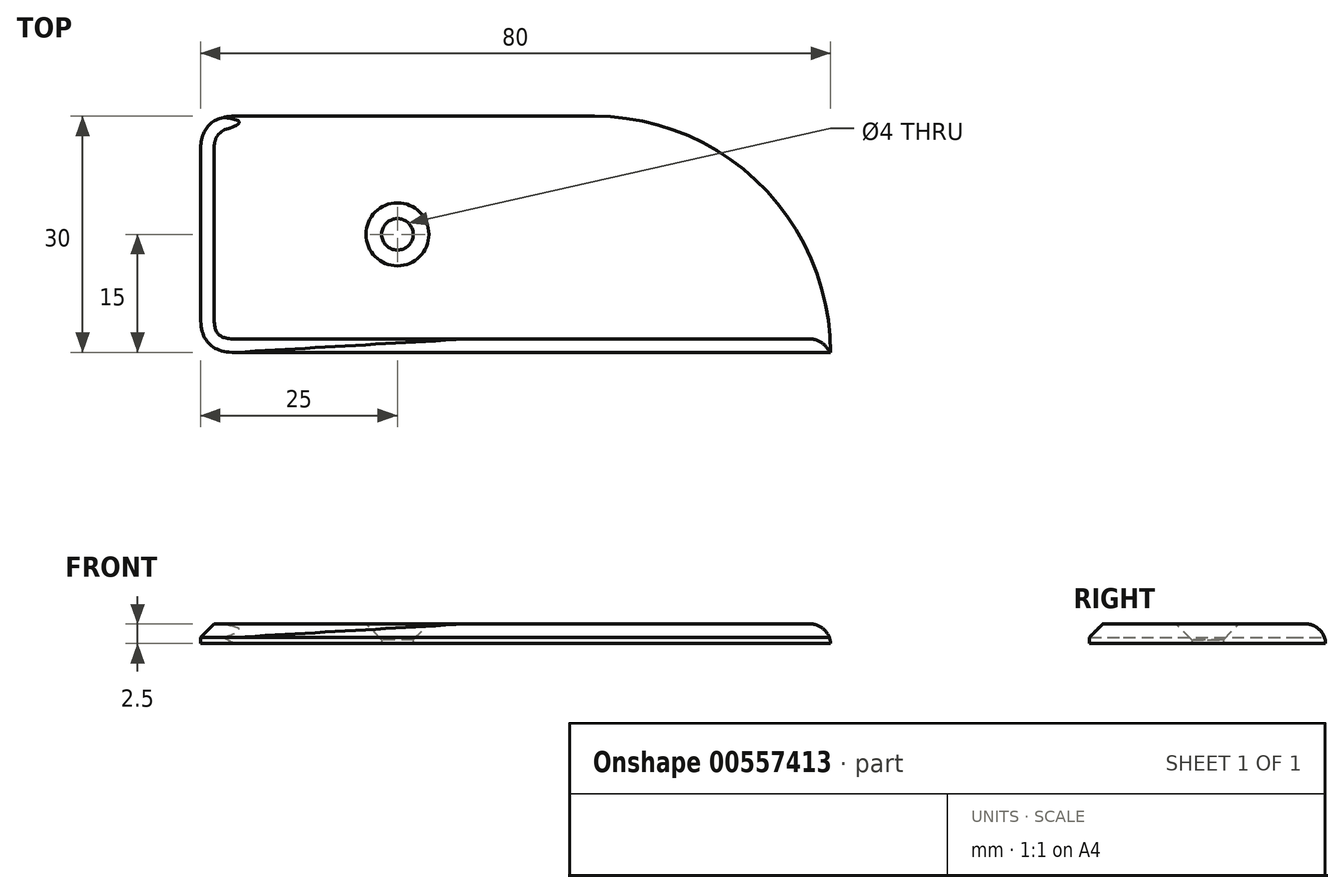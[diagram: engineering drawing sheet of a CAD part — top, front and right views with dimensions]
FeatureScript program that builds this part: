
annotation { "Feature Type Name" : "Feature", "Feature Type Description" : "" }
export const myFeature = defineFeature(function(context is Context, id is Id, definition is map)
    precondition{}
    {
        {
            var Q0;
            Q0=qCreatedBy(makeId("Top.planeOp"),FACE);
            var sketch = newSketch(context, id + "F0", { "sketchPlane" : qUnion([Q0])});
            skLineSegment(sketch, "E0.bottom", {"start": v(25, -15) * mm, "end": v(-25, -15) * mm});
            skLineSegment(sketch, "E0.top", {"start": v(25, 15) * mm, "end": v(-25, 15) * mm});
            skLineSegment(sketch, "E0.left", {"start": v(25, -15) * mm, "end": v(25, 15) * mm});
            skLineSegment(sketch, "E0.right", {"start": v(-25, -15) * mm, "end": v(-25, 15) * mm});
            skPoint(sketch, "E0.middle", {"position": v(0, 0) * mm});
            skLineSegment(sketch, "E1", {"start": v(25, -15) * mm, "end": v(55, -15) * mm});
            skArc(sketch, "E2", {"start": v(55, -15) * mm, "mid": v(46.21, 6.21) * mm, "end": v(25, 15) * mm});
            skCircle(sketch, "E3", {"center": v(0, 0) * mm, "radius": 2 * mm});
            skSolve(sketch);
        }
        {
            var Q0;
            Q0=makeQuery(id+"F0.imprint","IMPRINT",FACE,{"disambiguationData":[TD([[makeQuery(id+"F0.imprint","IMPRINT",EDGE,{"derivedFrom":sQuery(id+"F0.wireOp",EDGE,"E0.bottom")}),-1.0]])]});
            var Q1;
            Q1=makeQuery(id+"F0.imprint","IMPRINT",FACE,{"disambiguationData":[TD([[makeQuery(id+"F0.imprint","IMPRINT",EDGE,{"derivedFrom":sQuery(id+"F0.wireOp",EDGE,"E0.left")}),-1.0]])]});
            extrude(context, id + "F1", {"entities" : qUnion([Q0, Q1]), "depth" : 2.5 * mm, "offsetDistance" : 25 * mm});
        }
        {
            var Q0;
            Q0=makeQuery(id+"F1.opExtrude","SWEPT_EDGE",EDGE,{"disambiguationData":[OSD([sQuery(id+"F0.wireOp",EDGE,"E0.top"),sQuery(id+"F0.wireOp",EDGE,"E0.right")])]});
            var Q1;
            Q1=makeQuery(id+"F1.opExtrude","SWEPT_EDGE",EDGE,{"disambiguationData":[OSD([sQuery(id+"F0.wireOp",EDGE,"E0.bottom"),sQuery(id+"F0.wireOp",EDGE,"E0.right")])]});
            fillet(context, id + "F2", {"entities" : qUnion([Q0, Q1]), "radius" : 4.35 * mm, "tangentPropagation" : true, "rho" : 0.5, "crossSection" : FilletCrossSection.CONIC, "allowEdgeOverflow" : false});
        }
        {
            var Q0;
            Q0=makeQuery(id+"F1.opExtrude","CAP_EDGE",EDGE,{"disambiguationData":[OSD([sQuery(id+"F0.wireOp",EDGE,"E3")])],"isStart":false});
            chamfer(context, id + "F3", {"entities" : qUnion([Q0]), "chamferType" : ChamferType.OFFSET_ANGLE, "width" : 2 * mm, "oppositeDirection" : false, "angle" : 45 * degree, "tangentPropagation" : true});
        }
        {
            var Q0;
            Q0=makeQuery(id+"F1.opExtrude","CAP_EDGE",EDGE,{"disambiguationData":[OSD([sQuery(id+"F0.wireOp",EDGE,"E0.top")])],"isStart":false});
            var Q1;
            Q1=makeQuery(id+"F1.opExtrude","CAP_EDGE",EDGE,{"disambiguationData":[OSD([sQuery(id+"F0.wireOp",EDGE,"E2")])],"isStart":false});
            fillet(context, id + "F4", {"entities" : qUnion([Q0, Q1]), "radius" : 2.5 * mm, "rho" : 0.4, "crossSection" : FilletCrossSection.CONIC, "allowEdgeOverflow" : false});
        }
        {
            var Q0;
            Q0=makeQuery(id+"F1.opExtrude","CAP_EDGE",EDGE,{"disambiguationData":[OSD([sQuery(id+"F0.wireOp",EDGE,"E0.bottom"),sQuery(id+"F0.wireOp",EDGE,"E1")])],"isStart":false});
            chamfer(context, id + "F5", {"entities" : qUnion([Q0]), "width" : 1.7 * mm});
        }
        {
            var Q0;
            Q0=makeQuery(id+"F1.opExtrude","CAP_EDGE",EDGE,{"disambiguationData":[OSD([sQuery(id+"F0.wireOp",EDGE,"E0.right")])],"isStart":false});
            var Q1;
            {var subQ0=sQuery(id+"F0.wireOp",EDGE,"E0.right");var subQ1=sQuery(id+"F0.wireOp",EDGE,"E0.bottom");Q1=makeQuery(id+"F2.opFillet","BLEND_EDGE",EDGE,{"blendedFrom":[makeQuery(id+"F1.opExtrude","SWEPT_EDGE",EDGE,{"disambiguationData":[OSD([subQ1,subQ0])]}),makeQuery(id+"F1.opExtrude","CAP_FACE",FACE,{"disambiguationData":[OSD([subQ1,sQuery(id+"F0.wireOp",EDGE,"E0.top"),subQ0,sQuery(id+"F0.wireOp",EDGE,"E1"),sQuery(id+"F0.wireOp",EDGE,"E2"),sQuery(id+"F0.wireOp",EDGE,"E3")])],"isStart":false})],"blendedInto":[makeQuery(id+"F1.opExtrude","CAP_FACE",FACE,{"disambiguationData":[OSD([subQ1,sQuery(id+"F0.wireOp",EDGE,"E0.top"),subQ0,sQuery(id+"F0.wireOp",EDGE,"E1"),sQuery(id+"F0.wireOp",EDGE,"E2"),sQuery(id+"F0.wireOp",EDGE,"E3")])],"isStart":false})]});}
            var Q2;
            {var subQ0=sQuery(id+"F0.wireOp",EDGE,"E0.right");var subQ1=sQuery(id+"F0.wireOp",EDGE,"E0.top");Q2=makeQuery(id+"F2.opFillet","BLEND_EDGE",EDGE,{"blendedFrom":[makeQuery(id+"F1.opExtrude","SWEPT_EDGE",EDGE,{"disambiguationData":[OSD([subQ1,subQ0])]}),makeQuery(id+"F1.opExtrude","CAP_FACE",FACE,{"disambiguationData":[OSD([sQuery(id+"F0.wireOp",EDGE,"E0.bottom"),subQ1,subQ0,sQuery(id+"F0.wireOp",EDGE,"E1"),sQuery(id+"F0.wireOp",EDGE,"E2"),sQuery(id+"F0.wireOp",EDGE,"E3")])],"isStart":false})],"blendedInto":[makeQuery(id+"F1.opExtrude","CAP_FACE",FACE,{"disambiguationData":[OSD([sQuery(id+"F0.wireOp",EDGE,"E0.bottom"),subQ1,subQ0,sQuery(id+"F0.wireOp",EDGE,"E1"),sQuery(id+"F0.wireOp",EDGE,"E2"),sQuery(id+"F0.wireOp",EDGE,"E3")])],"isStart":false})]});}
            chamfer(context, id + "F6", {"entities" : qUnion([Q0, Q1, Q2]), "chamferType" : ChamferType.OFFSET_ANGLE, "width" : 1.7 * mm, "oppositeDirection" : false, "angle" : 45 * degree});
        }
    });
